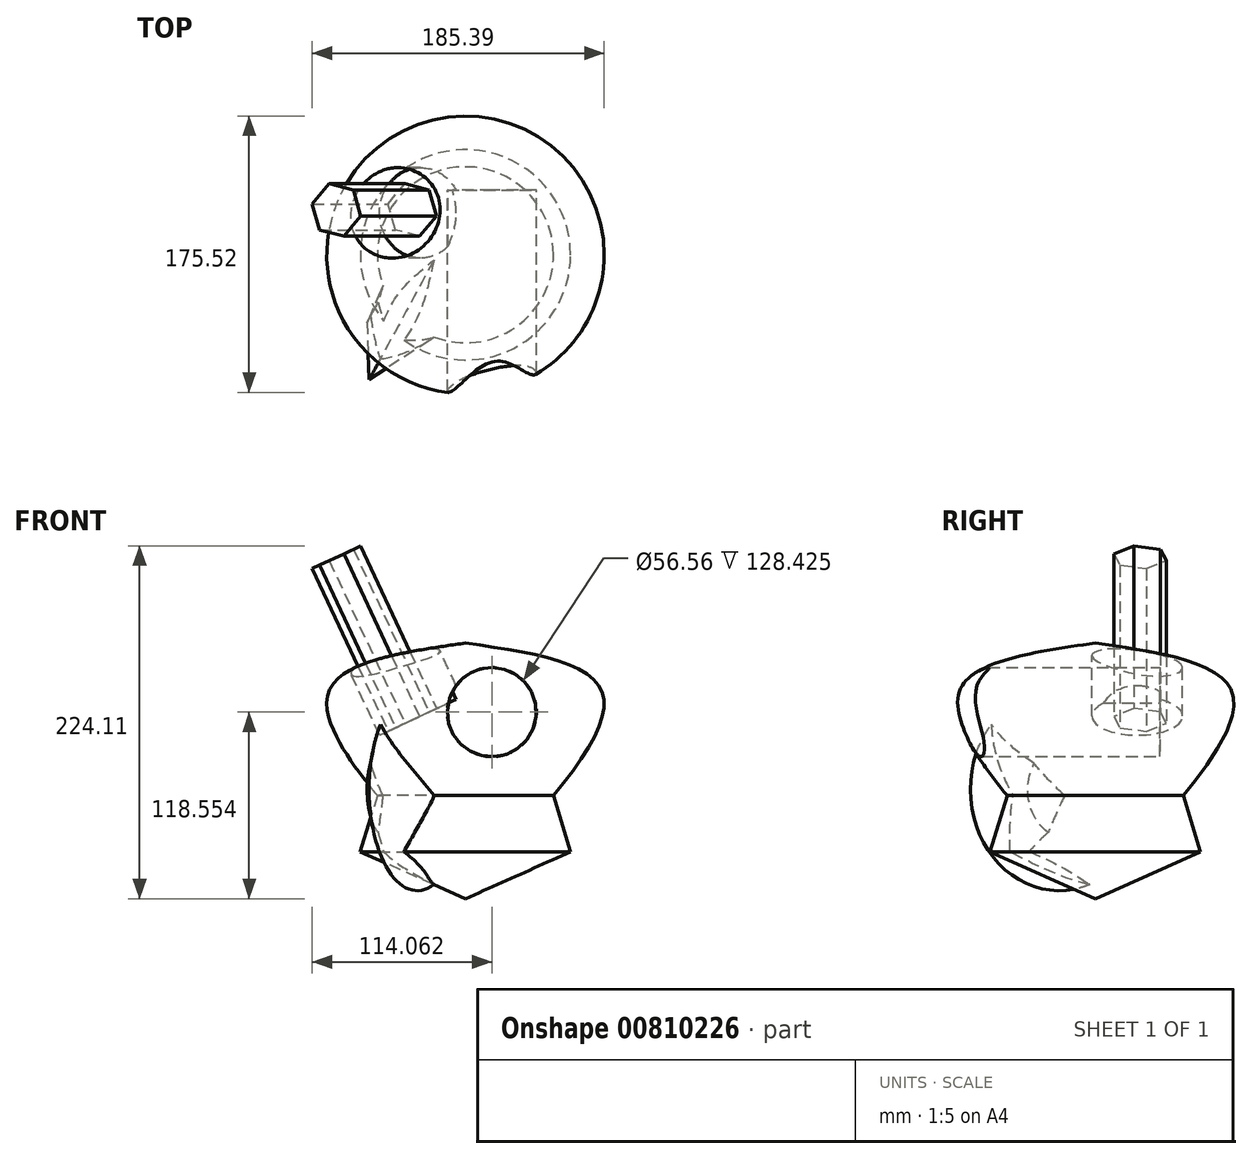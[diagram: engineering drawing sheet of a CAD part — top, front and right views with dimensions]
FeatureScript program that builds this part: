
annotation { "Feature Type Name" : "Feature", "Feature Type Description" : "" }
export const myFeature = defineFeature(function(context is Context, id is Id, definition is map)
    precondition{}
    {
        {
            var Q0;
            Q0=qCreatedBy(makeId("Front.planeOp"),FACE);
            var sketch = newSketch(context, id + "F0", { "sketchPlane" : qUnion([Q0])});
            skLineSegment(sketch, "E0", {"start": v(0, 93.07) * mm, "end": v(0, -65.08) * mm});
            skFitSpline(sketch, "E1", {"points": [v(0, 93.07) * mm, v(87.15, 61.2) * mm, v(0, -65.08) * mm], "startDerivative": vector(276.67, -39.7) * mm, "endDerivative": vector(-254.53, -267.13) * mm});
            skSolve(sketch);
        }
        {
            var Q0;
            Q0=makeQuery(id+"F0.imprint","IMPRINT",FACE,{"disambiguationData":[TD([[makeQuery(id+"F0.imprint","IMPRINT",EDGE,{"derivedFrom":sQuery(id+"F0.wireOp",EDGE,"E0")}),1.0]])]});
            var Q1;
            Q1=sQuery(id+"F0.wireOp",EDGE,"E0");
            revolve(context, id + "F1", {"surfaceOperationType" : NewSurfaceOperationType.NEW, "entities" : qUnion([Q0]), "axis" : qUnion([Q1]), "revolveType" : RevolveType.FULL});
        }
        {
            var Q0;
            Q0=qCreatedBy(makeId("Right.planeOp"),FACE);
            var sketch = newSketch(context, id + "F2", { "sketchPlane" : qUnion([Q0])});
            skLineSegment(sketch, "E2", {"start": v(0, -69.37) * mm, "end": v(0, 27.15) * mm});
            skLineSegment(sketch, "E3", {"start": v(0, 27.15) * mm, "end": v(54.72, 0) * mm});
            skLineSegment(sketch, "E4", {"start": v(54.72, 0) * mm, "end": v(66.79, -39.5) * mm});
            skLineSegment(sketch, "E5", {"start": v(66.79, -39.5) * mm, "end": v(0, -69.37) * mm});
            skSolve(sketch);
        }
        {
            var Q0;
            Q0 = qSketchRegion(id + "F2", true);
            var Q1;
            Q1=sQuery(id+"F2.wireOp",EDGE,"E2");
            revolve(context, id + "F3", {"operationType" : NewBodyOperationType.ADD, "surfaceOperationType" : NewSurfaceOperationType.NEW, "entities" : qUnion([Q0]), "axis" : qUnion([Q1]), "revolveType" : RevolveType.FULL});
        }
        {
            var Q0;
            Q0=qCreatedBy(makeId("Top.planeOp"),FACE);
            var sketch = newSketch(context, id + "F4", { "sketchPlane" : qUnion([Q0])});
            skLineSegment(sketch, "E6", {"start": v(0, -39.41) * mm, "end": v(0, 33.63) * mm});
            skLineSegment(sketch, "E7", {"start": v(0, 33.63) * mm, "end": v(-31.2, 14.76) * mm});
            skLineSegment(sketch, "E8", {"start": v(-31.2, 14.76) * mm, "end": v(-49.45, -12.63) * mm});
            skLineSegment(sketch, "E9", {"start": v(-49.45, -12.63) * mm, "end": v(0, -39.41) * mm});
            skSolve(sketch);
        }
        {
            var Q0;
            Q0 = qSketchRegion(id + "F4", true);
            var Q1;
            Q1=sQuery(id+"F4.wireOp",EDGE,"E9");
            revolve(context, id + "F5", {"operationType" : NewBodyOperationType.ADD, "surfaceOperationType" : NewSurfaceOperationType.NEW, "entities" : qUnion([Q0]), "axis" : qUnion([Q1]), "revolveType" : RevolveType.FULL});
        }
        {
            var Q0;
            Q0=qCreatedBy(makeId("Front.planeOp"),FACE);
            var sketch = newSketch(context, id + "F6", { "sketchPlane" : qUnion([Q0])});
            skCircle(sketch, "E10", {"center": v(16.77, 49.18) * mm, "radius": 28.28 * mm});
            skPoint(sketch, "E10.first.point", {"position": v(-10.31, 57.32) * mm});
            skPoint(sketch, "E10.second.point", {"position": v(45.04, 48.44) * mm});
            skPoint(sketch, "E10.third.point", {"position": v(-11.36, 52.1) * mm});
            skSolve(sketch);
        }
        {
            var Q0;
            Q0 = qSketchRegion(id + "F6", true);
            extrude(context, id + "F7", {"entities" : qUnion([Q0]), "operationType" : NewBodyOperationType.REMOVE, "depth" : 134 * mm, "offsetDistance" : 25 * mm, "hasSecondDirection" : true, "secondDirectionOppositeDirection" : true, "secondDirectionDepth" : 41 * mm});
        }
        {
            var Q0;
            Q0=qCreatedBy(makeId("Top.planeOp"),FACE);
            cPlane(context, id + "F8", {"entities" : qUnion([Q0]), "cplaneType" : CPlaneType.OFFSET, "offset" : 135 * mm, "width" : 150 * mm, "height" : 150 * mm});
        }
        {
            var Q0;
            Q0=qCreatedBy(id+"F8.planeOp",FACE);
            var sketch = newSketch(context, id + "F9", { "sketchPlane" : qUnion([Q0])});
            skLineSegment(sketch, "E11", {"start": v(0, 85.5) * mm, "end": v(0, -78.75) * mm});
            skSolve(sketch);
        }
        {
            var Q0;
            Q0=sQuery(id+"F9.wireOp",EDGE,"E11");
            cPlane(context, id + "F10", {"entities" : qUnion([Q0]), "cplaneType" : CPlaneType.LINE_ANGLE, "offset" : 15 * mm, "angle" : 25 * degree, "width" : 150 * mm, "height" : 150 * mm});
        }
        {
            var Q0;
            Q0=qCreatedBy(id+"F10.planeOp",FACE);
            var sketch = newSketch(context, id + "F11", { "sketchPlane" : qUnion([Q0])});
            skCircle(sketch, "E12", {"center": v(-6.12, -26.65) * mm, "radius": 28.72 * mm});
            skPoint(sketch, "E12.first.point", {"position": v(4.6, 0) * mm});
            skPoint(sketch, "E12.second.point", {"position": v(-6.1, -55.37) * mm});
            skPoint(sketch, "E12.third.point", {"position": v(17.62, -42.8) * mm});
            skSolve(sketch);
        }
        {
            var Q0;
            Q0=makeQuery(id+"F11.imprint","IMPRINT",FACE,{"disambiguationData":[TD([[makeQuery(id+"F11.imprint","IMPRINT",EDGE,{"derivedFrom":sQuery(id+"F11.wireOp",EDGE,"E12")}),1.0]])]});
            extrude(context, id + "F12", {"entities" : qUnion([Q0]), "operationType" : NewBodyOperationType.REMOVE, "depth" : 68 * mm, "offsetDistance" : 25 * mm});
        }
        {
            var Q0;
            Q0=makeQuery(id+"F12.boolean.opBoolean","COPY",FACE,{"derivedFrom":makeQuery(id+"F12.opExtrude","CAP_FACE",FACE,{"disambiguationData":[OSD([sQuery(id+"F11.wireOp",EDGE,"E12")])],"isStart":false})});
            var sketch = newSketch(context, id + "F13", { "sketchPlane" : qUnion([Q0])});
            skCircle(sketch, "E13.cCircle", {"center": v(-11.86, 28.49) * mm, "radius": 17.42 * mm, "construction": true});
            skLineSegment(sketch, "E13.0", {"start": v(0, 41.25) * mm, "end": v(5.13, 24.6) * mm});
            skLineSegment(sketch, "E13.1", {"start": v(5.13, 24.6) * mm, "end": v(-6.73, 11.83) * mm});
            skLineSegment(sketch, "E13.2", {"start": v(-6.73, 11.83) * mm, "end": v(-23.72, 15.72) * mm});
            skLineSegment(sketch, "E13.3", {"start": v(-23.72, 15.72) * mm, "end": v(-28.84, 32.37) * mm});
            skLineSegment(sketch, "E13.4", {"start": v(-28.84, 32.37) * mm, "end": v(-16.98, 45.14) * mm});
            skLineSegment(sketch, "E13.5", {"start": v(-16.98, 45.14) * mm, "end": v(0, 41.25) * mm});
            skSolve(sketch);
        }
        {
            var Q0;
            Q0=makeQuery(id+"F13.imprint","IMPRINT",FACE,{"disambiguationData":[TD([[makeQuery(id+"F13.imprint","IMPRINT",EDGE,{"derivedFrom":sQuery(id+"F13.wireOp",EDGE,"E13.0")}),-1.0]])]});
            extrude(context, id + "F14", {"entities" : qUnion([Q0]), "operationType" : NewBodyOperationType.ADD, "depth" : 114 * mm, "offsetDistance" : 25 * mm});
        }
    });
